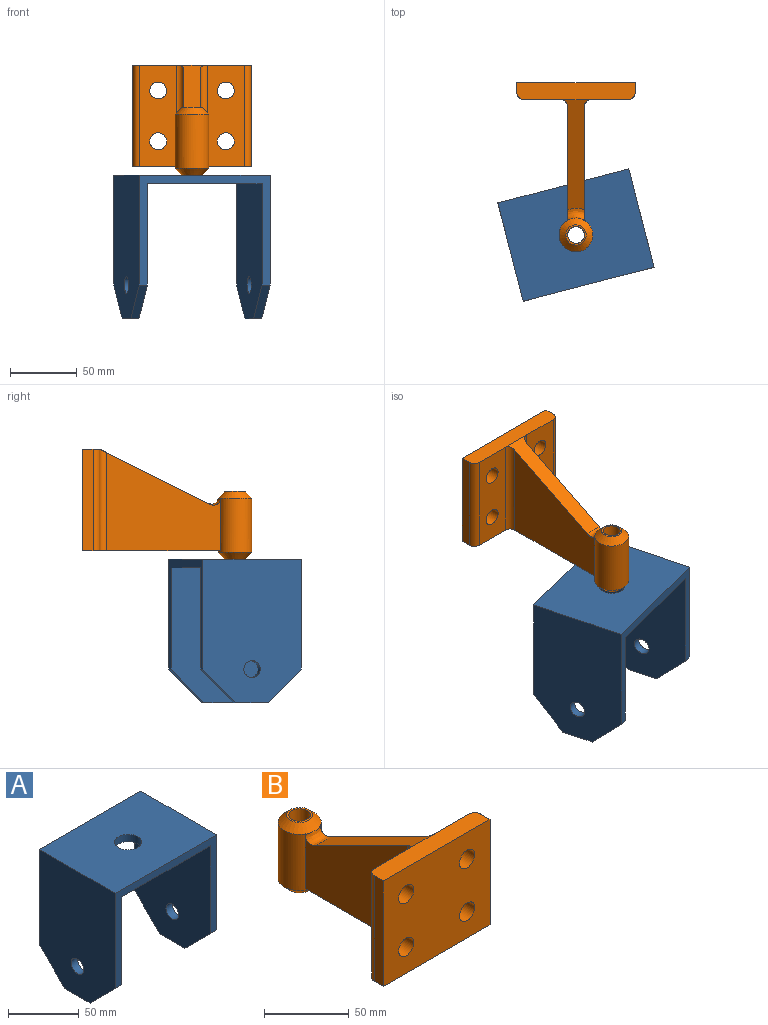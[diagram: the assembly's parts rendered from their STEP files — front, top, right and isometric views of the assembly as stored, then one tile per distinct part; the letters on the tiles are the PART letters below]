
ASSEMBLY  parts=2 mates=1
PART A: 17 faces, bbox 101.6x76.2x108 mm
  f0: plane 101.6x82.55mm, normal (0,-1,0), area 1612.9mm2, adj f1,f5,f6,f7,f8,f9,f12,f13
  f1: plane 25.4x25.4mm, normal (0,-0.71,-0.71), area 228.1mm2, adj f0,f2,f5,f6
  f2: plane 25.4x6.35mm, normal (0,0,-1), area 161.3mm2, adj f1,f3,f5,f6
  f3: plane 25.4x25.4mm, normal (0,0.71,-0.71), area 228.1mm2, adj f2,f4,f5,f6
  f4: plane 101.6x82.55mm, normal (0,1,0), area 1612.9mm2, adj f3,f5,f6,f7,f8,f11,f12,f13
  f5: plane 101.6x76.2mm, normal (1,0,0), area 6970.1mm2, adj f0,f1,f2,f3,f4,f7,f15
  f6: plane 107.95x76.2mm, normal (-1,0,0), area 7454mm2, adj f0,f1,f2,f3,f4,f8,f15
  f7: plane 88.9x76.2mm, normal (0,0,-1), area 6489.2mm2, adj f0,f4,f5,f12,f16
  f8: plane 101.6x76.2mm, normal (0,0,1), area 7456.9mm2, adj f0,f4,f6,f13,f16
  f9: plane 25.4x25.4mm, normal (0,-0.71,-0.71), area 228.1mm2, adj f0,f10,f12,f13
  f10: plane 25.4x6.35mm, normal (0,0,-1), area 161.3mm2, adj f9,f11,f12,f13
  f11: plane 25.4x25.4mm, normal (0,0.71,-0.71), area 228.1mm2, adj f4,f10,f12,f13
  f12: plane 101.6x76.2mm, normal (-1,0,0), area 6970.1mm2, adj f0,f4,f7,f9,f10,f11,f14
  f13: plane 107.95x76.2mm, normal (1,0,0), area 7454mm2, adj f0,f4,f8,f9,f10,f11,f14
  f14: cylinder r=6.35mm len=12.7mm, axis (-1,0,0), area 253.4mm2, adj f12,f13
  f15: cylinder r=6.35mm len=12.7mm, axis (-1,0,0), area 253.4mm2, adj f5,f6
  f16: cylinder r=9.53mm len=19.05mm, axis (0,0,1), area 380mm2, adj f7,f8
PART B: 25 faces, bbox 90x128.1x83.6 mm
  f0: plane 83.79x42.43mm, normal (0,0.45,0.89), area 1175.8mm2, adj f2,f3,f5,f20,f21,f24
  f1: plane 103.3x88.9mm, normal (0,0,-1), area 2265.1mm2, adj f2,f3,f4,f6,f10,f12,f13,f14
  f2: plane 85.52x73.66mm, normal (1,0,0), area 4486.9mm2, adj f0,f1,f16,f21,f24
  f3: plane 85.52x73.66mm, normal (-1,0,0), area 4486.9mm2, adj f0,f1,f16,f20,f24
  f4: plane 76.2x27.94mm, normal (0,1,0), area 1875.7mm2, adj f1,f5,f7,f11,f15,f20
  f5: plane 88.9x12.7mm, normal (0,0,1), area 1118mm2, adj f0,f4,f6,f10,f12,f13,f14,f15
  f6: plane 76.2x7.62mm, normal (-1,0,0), area 580.6mm2, adj f1,f5,f12,f15
  f7: cylinder r=6.35mm len=12.7mm, axis (0,1,0), area 506.7mm2, adj f4,f12
  f8: cylinder r=6.35mm len=12.7mm, axis (0,1,0), area 506.7mm2, adj f12,f13
  f9: cylinder r=6.35mm len=12.7mm, axis (0,1,0), area 506.7mm2, adj f12,f13
  f10: plane 76.2x7.62mm, normal (1,0,0), area 580.6mm2, adj f1,f5,f12,f14
  f11: cylinder r=6.35mm len=12.7mm, axis (0,1,0), area 506.7mm2, adj f4,f12
  f12: plane 88.9x76.2mm, normal (0,-1,0), area 6267.5mm2, adj f1,f5,f6,f7,f8,f9,f10,f11
  f13: plane 76.2x27.94mm, normal (0,1,0), area 1875.7mm2, adj f1,f5,f8,f9,f14,f21
  f14: cylinder r=5.08mm len=76.2mm, axis (0,0,1), area 608mm2, adj f1,f5,f10,f13
  f15: cylinder r=5.08mm len=76.2mm, axis (0,0,-1), area 608mm2, adj f1,f4,f5,f6
  f16: cylinder r=12.7mm len=40.64mm, axis (0,0,-1), area 2720.5mm2, adj f1,f2,f3,f22,f23,f24
  f17: plane 15.24x15.24mm, normal (0,0,1), area 55.7mm2, adj f19,f22
  f18: plane 15.24x15.24mm, normal (0,0,-1), area 55.7mm2, adj f19,f23
  f19: cylinder r=6.35mm len=50.8mm, axis (0,0,1), area 2026.8mm2, adj f17,f18
  f20: cylinder r=5.08mm len=76.2mm, axis (0,0,1), area 597.9mm2, adj f0,f1,f3,f4
  f21: cylinder r=5.08mm len=76.2mm, axis (0,0,-1), area 597.9mm2, adj f0,f1,f2,f13
  f22: cone r=12.7mm half-angle=45deg, axis (0,0,-1), area 458.6mm2, adj f16,f17,f24
  f23: cone r=7.62mm half-angle=45deg, axis (0,0,1), area 458.6mm2, adj f16,f18
  f24: bspline ~18.39x9.18mm, area 136.4mm2, adj f0,f2,f3,f16,f22
PLACE A rot(axis=(0,0,-1),165.4deg) t=(233.05,-773.33,-135.2)mm
PLACE B rot(axis=(0,0,-1),180deg) t=(233.05,-719.76,-13.21)mm fixed
MATE revolute A.f16 <-> B.f16  axis (0,0,1) through (233.05,-773.33,-62.46)mm
